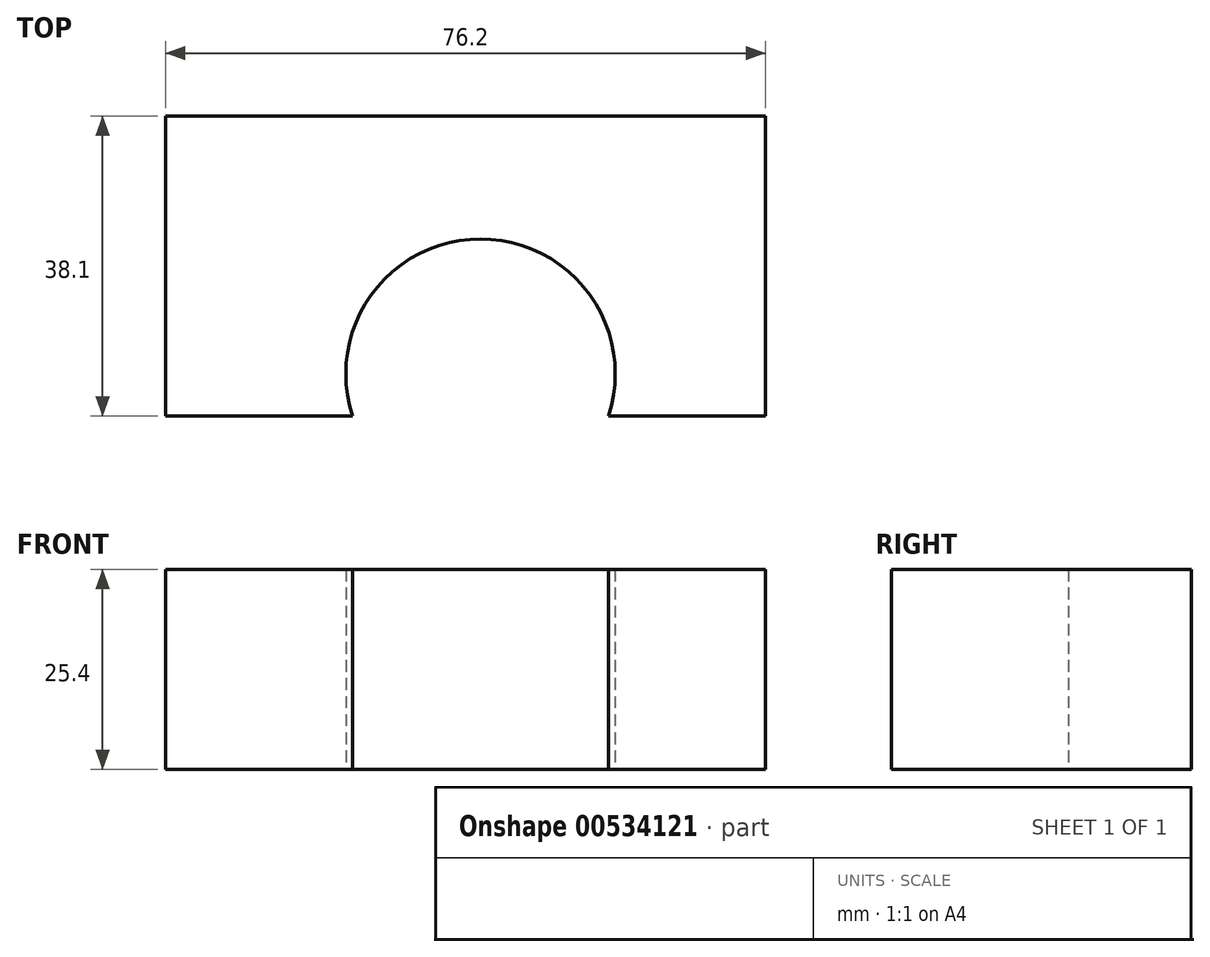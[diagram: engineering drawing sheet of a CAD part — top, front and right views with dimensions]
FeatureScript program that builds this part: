
annotation { "Feature Type Name" : "Feature", "Feature Type Description" : "" }
export const myFeature = defineFeature(function(context is Context, id is Id, definition is map)
    precondition{}
    {
        {
            var Q0;
            Q0=qCreatedBy(makeId("Top.planeOp"),FACE);
            var sketch = newSketch(context, id + "F0", { "sketchPlane" : qUnion([Q0])});
            skLineSegment(sketch, "E0.bottom", {"start": v(-42.71, 38.1) * mm, "end": v(33.49, 38.1) * mm});
            skLineSegment(sketch, "E0.top", {"start": v(-42.71, 0) * mm, "end": v(33.49, 0) * mm});
            skLineSegment(sketch, "E0.left", {"start": v(-42.71, 38.1) * mm, "end": v(-42.71, 0) * mm});
            skLineSegment(sketch, "E0.right", {"start": v(33.49, 38.1) * mm, "end": v(33.49, 0) * mm});
            skArc(sketch, "E1", {"start": v(13.54, 0) * mm, "mid": v(-2.7, 22.49) * mm, "end": v(-18.95, 0) * mm});
            skSolve(sketch);
        }
        {
            var Q0;
            Q0=qSketchRegion(id+"F0",true);
            extrude(context, id + "F1", {"entities" : qUnion([Q0]), "depth" : 25.4 * mm, "offsetDistance" : 25.4 * mm});
        }
        {
            var Q0;
            {var subQ0=sQuery(id+"F0.wireOp",EDGE,"E1");Q0=makeQuery(id+"F0.imprint","IMPRINT",FACE,{"disambiguationData":[TD([[makeQuery(id+"F0.imprint","IMPRINT",EDGE,{"derivedFrom":subQ0}),1.0]])]});}
            extrude(context, id + "F2", {"entities" : qUnion([Q0]), "operationType" : NewBodyOperationType.REMOVE, "depth" : 25.4 * mm, "offsetDistance" : 25.4 * mm});
        }
    });
